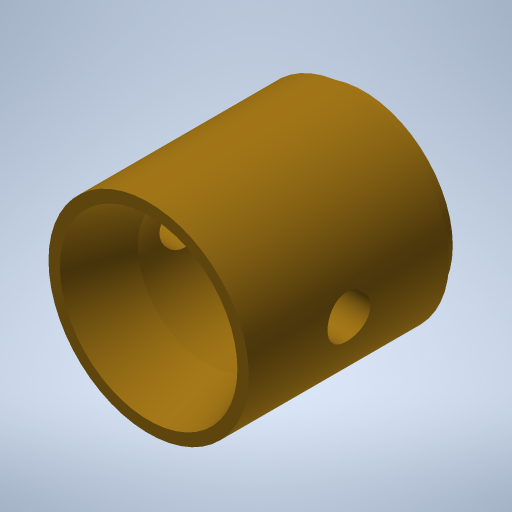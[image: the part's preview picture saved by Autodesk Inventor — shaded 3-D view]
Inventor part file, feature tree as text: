
AUTODESK INVENTOR PART (.ipt)
format: ipt  version: 2024 (Build 280153000, 153)  size: 404,992 bytes
history: native  units: mm (DEFAULTED — no unit token found)
features: other x9, sketch x2, plane x1, hole x1
ambient origin geometry x1: Ursprung
bodies: Volumenkörper1 (feature_tree)
feature tree (13):
  other  "Drehung1"
  plane  "Arbeitsebene1"
  sketch  "Skizze2"  dims[d2=14.0mm d3=12.4mm d4=1.0mm d6=3.490659mm d7=10.297443mm d8=11.0mm d9=15.0mm d10=90.0deg d12=-7.0mm d13=7.0mm d14=3.0mm d15=6.0mm d16=4.0mm d17=2.0mm d18=14.3117mm d19=8.0mm d20=20.594885mm]
  other  "Mittelebene"
  hole  "Bohrung1"  [1 undecoded]
  other  "YZ Ebene"
  other  "XZ Ebene"
  other  "XY Ebene"
  other  "X Achse"
  other  "Y Achse"
  other  "Z Achse"
  other  "Mittelpunkt"
  sketch  "Skizze1"  dims[d0=12.5mm d1=9.5mm]
note: 1 required parameter value undecoded (feature->parameter linkage not recoverable at this tier; creation-order binding heuristic only, values carry confidence <= 0.55)
